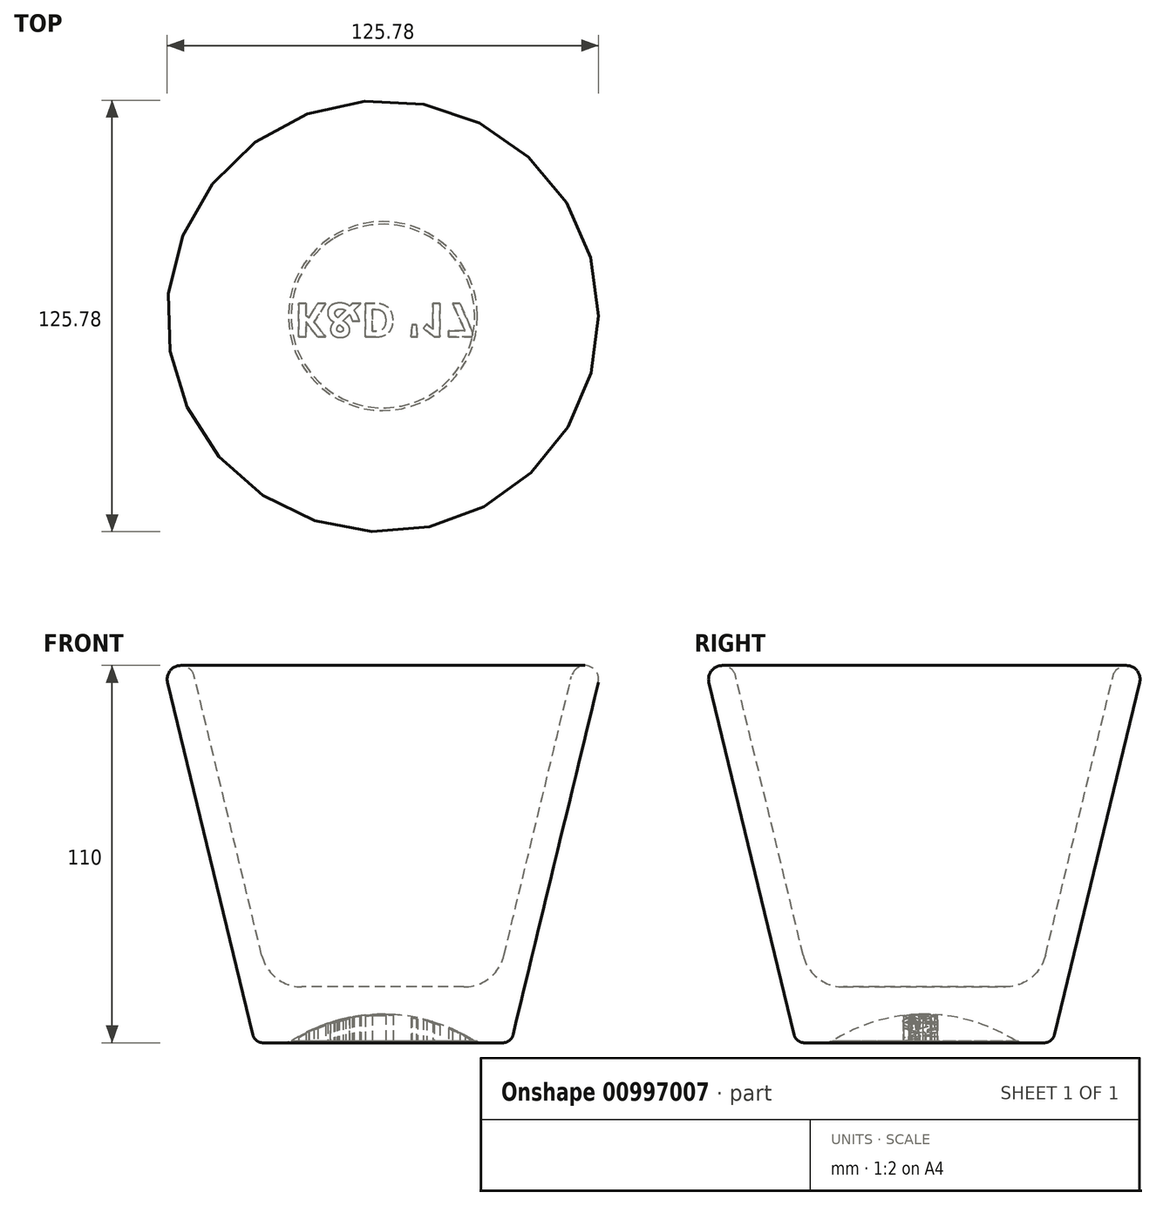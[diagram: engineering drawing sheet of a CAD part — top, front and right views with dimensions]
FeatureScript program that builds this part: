
annotation { "Feature Type Name" : "Feature", "Feature Type Description" : "" }
export const myFeature = defineFeature(function(context is Context, id is Id, definition is map)
    precondition{}
    {
        {
            var Q0;
            Q0=qCreatedBy(makeId("Right.planeOp"),FACE);
            var sketch = newSketch(context, id + "F0", { "sketchPlane" : qUnion([Q0])});
            skLineSegment(sketch, "E0", {"start": v(-27.54, 0) * mm, "end": v(-35, 0) * mm});
            skLineSegment(sketch, "E1", {"start": v(-37.92, 2.3) * mm, "end": v(-62.78, 105.06) * mm});
            skLineSegment(sketch, "E2", {"start": v(-55, 106.94) * mm, "end": v(-35.3, 25.48) * mm});
            skLineSegment(sketch, "E3", {"start": v(-23.63, 16.3) * mm, "end": v(0, 16.3) * mm});
            skLineSegment(sketch, "E4", {"start": v(0, 16.3) * mm, "end": v(0, 0) * mm});
            skLineSegment(sketch, "E5", {"start": v(-62.78, 105.06) * mm, "end": v(-55, 106.94) * mm, "construction": true});
            skArc(sketch, "E6", {"start": v(-55, 106.94) * mm, "mid": v(-59.83, 109.89) * mm, "end": v(-62.78, 105.06) * mm});
            skArc(sketch, "E7", {"start": v(0, 8.3) * mm, "mid": v(-14.38, 6.18) * mm, "end": v(-27.54, 0) * mm});
            skLineSegment(sketch, "E8.MirrorCS", {"start": v(62.78, 105.06) * mm, "end": v(55, 106.94) * mm, "construction": true});
            skArc(sketch, "E9.MirrorCS", {"start": v(55, 106.94) * mm, "mid": v(59.83, 109.89) * mm, "end": v(62.78, 105.06) * mm});
            skLineSegment(sketch, "E10.MirrorCS", {"start": v(27.54, 0) * mm, "end": v(35, 0) * mm});
            skArc(sketch, "E11.MirrorCS", {"start": v(0, 8.3) * mm, "mid": v(14.38, 6.18) * mm, "end": v(27.54, 0) * mm});
            skLineSegment(sketch, "E12.MirrorCS", {"start": v(37.92, 2.3) * mm, "end": v(62.78, 105.06) * mm});
            skLineSegment(sketch, "E13.MirrorCS", {"start": v(55, 106.94) * mm, "end": v(35.3, 25.48) * mm});
            skLineSegment(sketch, "E14.MirrorCS", {"start": v(23.63, 16.3) * mm, "end": v(0, 16.3) * mm});
            skPoint(sketch, "E15.visualSharp", {"position": v(33.07, 16.3) * mm});
            skArc(sketch, "E15.filletArc", {"start": v(23.63, 16.3) * mm, "mid": v(31.05, 18.87) * mm, "end": v(35.3, 25.48) * mm});
            skPoint(sketch, "E16.visualSharp", {"position": v(-33.07, 16.3) * mm});
            skArc(sketch, "E16.filletArc", {"start": v(-35.3, 25.48) * mm, "mid": v(-31.05, 18.87) * mm, "end": v(-23.63, 16.3) * mm});
            skPoint(sketch, "E17.visualSharp", {"position": v(37.36, 0) * mm});
            skArc(sketch, "E17.filletArc", {"start": v(35, 0) * mm, "mid": v(36.85, 0.64) * mm, "end": v(37.92, 2.3) * mm});
            skPoint(sketch, "E18.visualSharp", {"position": v(-37.36, 0) * mm});
            skArc(sketch, "E18.filletArc", {"start": v(-37.92, 2.3) * mm, "mid": v(-36.85, 0.64) * mm, "end": v(-35, 0) * mm});
            skSolve(sketch);
        }
        {
            var Q0;
            Q0=makeQuery(id+"F0.imprint","IMPRINT",FACE,{"disambiguationData":[TD([[makeQuery(id+"F0.imprint","IMPRINT",EDGE,{"derivedFrom":sQuery(id+"F0.wireOp",EDGE,"E0")}),-1.0]])]});
            var Q1;
            Q1=sQuery(id+"F0.wireOp",EDGE,"E4");
            revolve(context, id + "F1", {"surfaceOperationType" : NewSurfaceOperationType.NEW, "entities" : qUnion([Q0]), "axis" : qUnion([Q1]), "revolveType" : RevolveType.FULL});
        }
        {
            var Q0;
            Q0=makeQuery(id+"F1.opRevolve","SWEPT_FACE",FACE,{"disambiguationData":[OSD([sQuery(id+"F0.wireOp",EDGE,"E0")])]});
            var sketch = newSketch(context, id + "F2", { "sketchPlane" : qUnion([Q0])});
            skText(sketch, "E19", { "text": "K&D \'17", "fontName": "OpenSans-Bold.ttf"});
            const initialGuessF2  = {"E19": [-0.02574, -0.00368, 1, 0, 0.00986]};
            skSetInitialGuess(sketch, initialGuessF2);
            skSolve(sketch);
        }
        {
            var Q0;
            Q0 = qSketchRegion(id + "F2", true);
            extrude(context, id + "F3", {"entities" : qUnion([Q0]), "operationType" : NewBodyOperationType.ADD, "endBound" : BoundingType.UP_TO_NEXT, "oppositeDirection" : true, "depth" : 25 * mm, "offsetDistance" : 25 * mm});
        }
        {
            var Q0;
            Q0=makeQuery(id+"F1.opRevolve","SWEPT_FACE",FACE,{"disambiguationData":[OSD([sQuery(id+"F0.wireOp",EDGE,"E0")])]});
            var sketch = newSketch(context, id + "F4", { "sketchPlane" : qUnion([Q0])});
            skCircle(sketch, "E20.0", {"center": v(0, 0) * mm, "radius": 27.54 * mm});
            skSolve(sketch);
        }
        {
            var Q0;
            Q0=makeQuery(id+"F4.imprint","IMPRINT",FACE,{"disambiguationData":[TD([[makeQuery(id+"F4.imprint","IMPRINT",EDGE,{"derivedFrom":sQuery(id+"F4.wireOp",EDGE,"E20.0")}),-1.0]])]});
            extrude(context, id + "F5", {"entities" : qUnion([Q0]), "operationType" : NewBodyOperationType.REMOVE, "oppositeDirection" : true, "depth" : .5 * mm, "offsetDistance" : 25 * mm});
        }
    });
